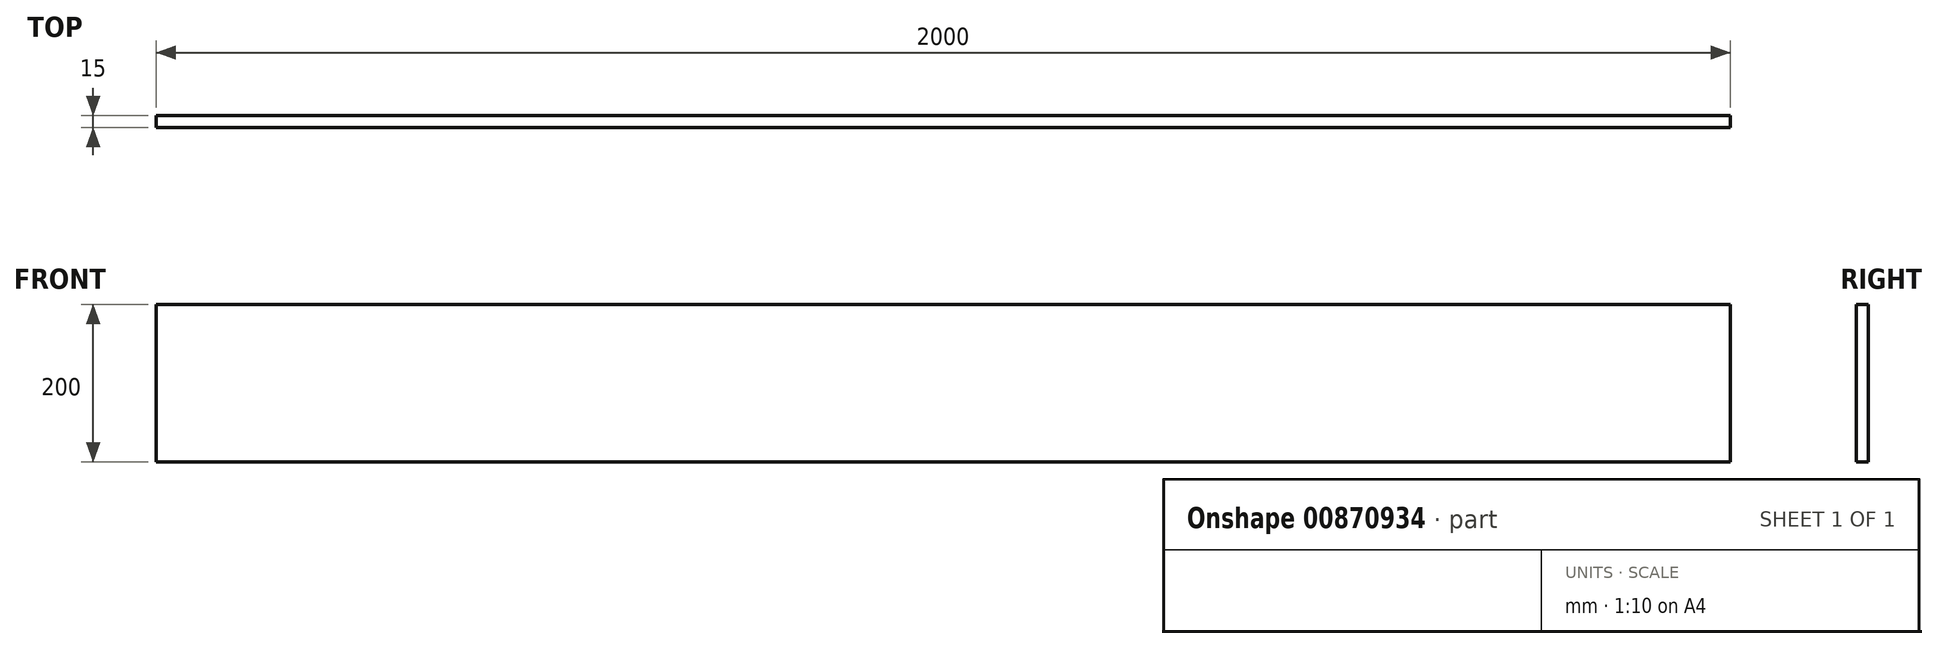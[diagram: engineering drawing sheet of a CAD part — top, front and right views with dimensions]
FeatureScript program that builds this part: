
annotation { "Feature Type Name" : "Feature", "Feature Type Description" : "" }
export const myFeature = defineFeature(function(context is Context, id is Id, definition is map)
    precondition{}
    {
        {
            var Q0;
            Q0=qCreatedBy(makeId("Front.planeOp"),FACE);
            var sketch = newSketch(context, id + "F0", { "sketchPlane" : qUnion([Q0])});
            skLineSegment(sketch, "E0.bottom", {"start": v(-1000, 100) * mm, "end": v(1000, 100) * mm});
            skLineSegment(sketch, "E0.top", {"start": v(-1000, -100) * mm, "end": v(1000, -100) * mm});
            skLineSegment(sketch, "E0.left", {"start": v(-1000, 100) * mm, "end": v(-1000, -100) * mm});
            skLineSegment(sketch, "E0.right", {"start": v(1000, 100) * mm, "end": v(1000, -100) * mm});
            skPoint(sketch, "E0.middle", {"position": v(0, 0) * mm});
            skSolve(sketch);
        }
        {
            var Q0;
            Q0 = qSketchRegion(id + "F0", true);
            extrude(context, id + "F1", {"entities" : qUnion([Q0]), "depth" : 15 * mm, "offsetDistance" : 25 * mm});
        }
    });
